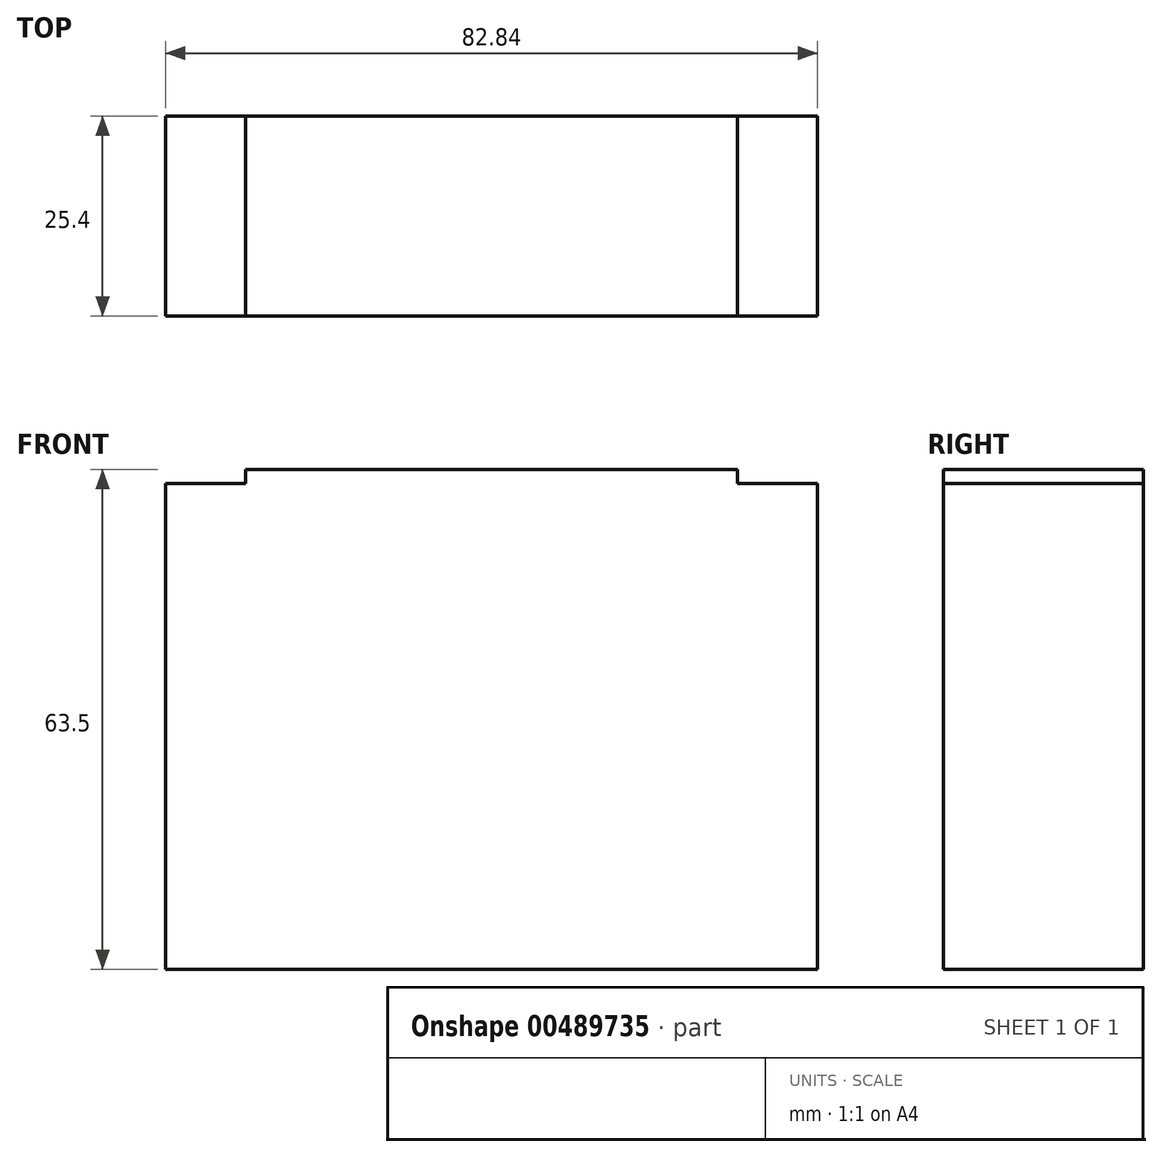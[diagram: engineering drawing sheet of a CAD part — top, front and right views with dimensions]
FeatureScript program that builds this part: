
annotation { "Feature Type Name" : "Feature", "Feature Type Description" : "" }
export const myFeature = defineFeature(function(context is Context, id is Id, definition is map)
    precondition{}
    {
        {
            var Q0;
            Q0=qCreatedBy(makeId("Front.planeOp"),FACE);
            var sketch = newSketch(context, id + "F0", { "sketchPlane" : qUnion([Q0])});
            skLineSegment(sketch, "E0.bottom", {"start": v(-30.21, 1.78) * mm, "end": v(32.27, 1.78) * mm});
            skLineSegment(sketch, "E0.top", {"start": v(-40.4, -61.72) * mm, "end": v(42.43, -61.72) * mm});
            skLineSegment(sketch, "E0.left", {"start": v(-40.4, 0) * mm, "end": v(-40.4, -61.72) * mm});
            skLineSegment(sketch, "E0.right", {"start": v(42.43, 0) * mm, "end": v(42.43, -61.72) * mm});
            skLineSegment(sketch, "E1.top", {"start": v(-40.4, 0) * mm, "end": v(-30.21, 0) * mm});
            skLineSegment(sketch, "E1.right", {"start": v(-30.21, 1.78) * mm, "end": v(-30.21, 0) * mm});
            skLineSegment(sketch, "E2.top", {"start": v(42.43, 0) * mm, "end": v(32.27, 0) * mm});
            skLineSegment(sketch, "E2.right", {"start": v(32.27, 1.78) * mm, "end": v(32.27, 0) * mm});
            skSolve(sketch);
        }
        {
            var Q0;
            Q0=makeQuery(id+"F0.imprint","IMPRINT",FACE,{"disambiguationData":[TD([[makeQuery(id+"F0.imprint","IMPRINT",EDGE,{"derivedFrom":sQuery(id+"F0.wireOp",EDGE,"E0.bottom")}),-1.0]])]});
            extrude(context, id + "F1", {"entities" : qUnion([Q0]), "depth" : 25.4 * mm});
        }
    });
